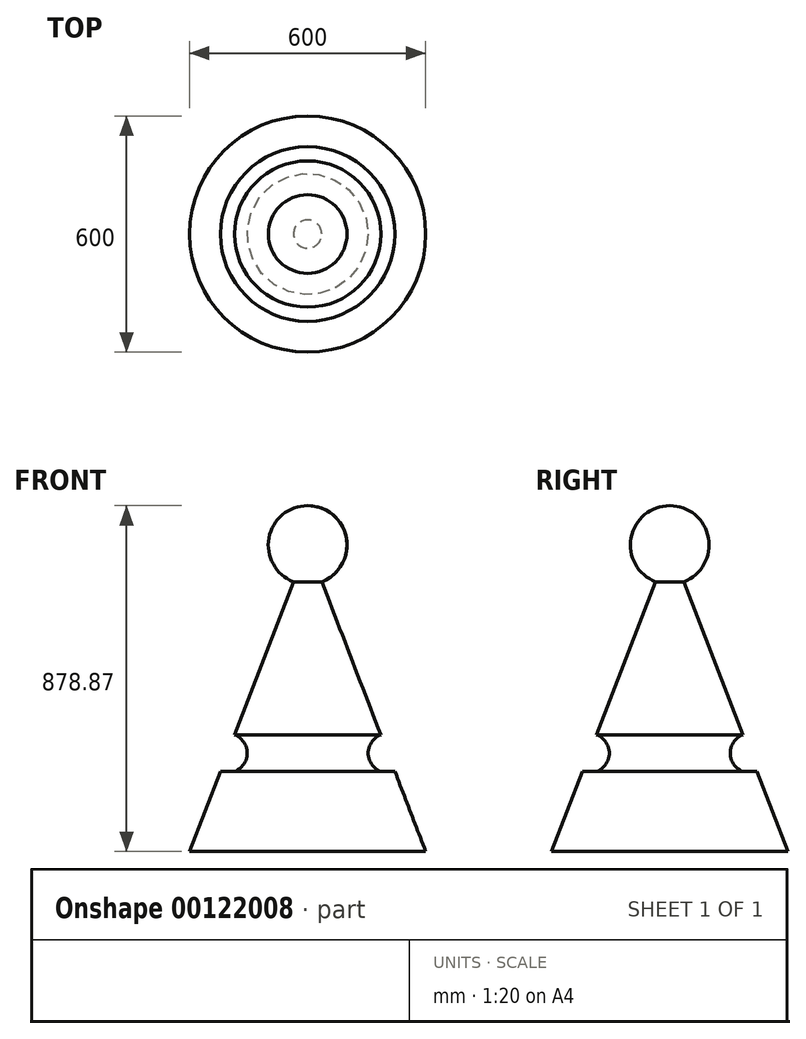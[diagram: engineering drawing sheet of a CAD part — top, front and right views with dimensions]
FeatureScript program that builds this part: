
annotation { "Feature Type Name" : "Feature", "Feature Type Description" : "" }
export const myFeature = defineFeature(function(context is Context, id is Id, definition is map)
    precondition{}
    {
        {
            var Q0;
            Q0=qCreatedBy(makeId("Front.planeOp"),FACE);
            var sketch = newSketch(context, id + "F0", { "sketchPlane" : qUnion([Q0])});
            skLineSegment(sketch, "E0", {"start": v(0, 293.94) * mm, "end": v(0, -362.94) * mm, "construction": true});
            skArc(sketch, "E1", {"start": v(0, 493.94) * mm, "mid": v(-98.32, 412.22) * mm, "end": v(-35.94, 300.63) * mm});
            skLineSegment(sketch, "E2", {"start": v(0, 293.94) * mm, "end": v(0, 15.5) * mm});
            skLineSegment(sketch, "E3", {"start": v(-300, -384.93) * mm, "end": v(0, -384.93) * mm});
            skPoint(sketch, "E4.end.orphan", {"position": v(0, -181.55) * mm});
            skLineSegment(sketch, "E5", {"start": v(0, -384.93) * mm, "end": v(0, -181.55) * mm});
            skPoint(sketch, "E6.end.orphan", {"position": v(-154.6, -181.55) * mm});
            skLineSegment(sketch, "E7", {"start": v(-35.94, 300.63) * mm, "end": v(-185.74, -88.27) * mm});
            skArc(sketch, "E8", {"start": v(-185.72, -181.58) * mm, "mid": v(-153.7, -134.92) * mm, "end": v(-185.74, -88.27) * mm});
            skPoint(sketch, "E9.orphan", {"position": v(0, -134.93) * mm});
            skLineSegment(sketch, "E10", {"start": v(-221.68, -181.59) * mm, "end": v(-185.72, -181.58) * mm});
            skPoint(sketch, "E11.orphan", {"position": v(0, 485.78) * mm});
            skLineSegment(sketch, "E12.trimOffspring", {"start": v(-221.68, -181.59) * mm, "end": v(-300, -384.93) * mm});
            skLineSegment(sketch, "E13", {"start": v(-35.94, 300.63) * mm, "end": v(0, 300.63) * mm});
            skLineSegment(sketch, "E14", {"start": v(0, 293.94) * mm, "end": v(0, 300.63) * mm});
            skLineSegment(sketch, "E15", {"start": v(0, 493.94) * mm, "end": v(0, -384.93) * mm});
            skSolve(sketch);
        }
        {
            var Q0;
            Q0 = qSketchRegion(id + "F0", true);
            var Q1;
            Q1=sQuery(id+"F0.wireOp",EDGE,"E15");
            revolve(context, id + "F1", {"entities" : qUnion([Q0]), "axis" : qUnion([Q1]), "revolveType" : RevolveType.FULL});
        }
    });
